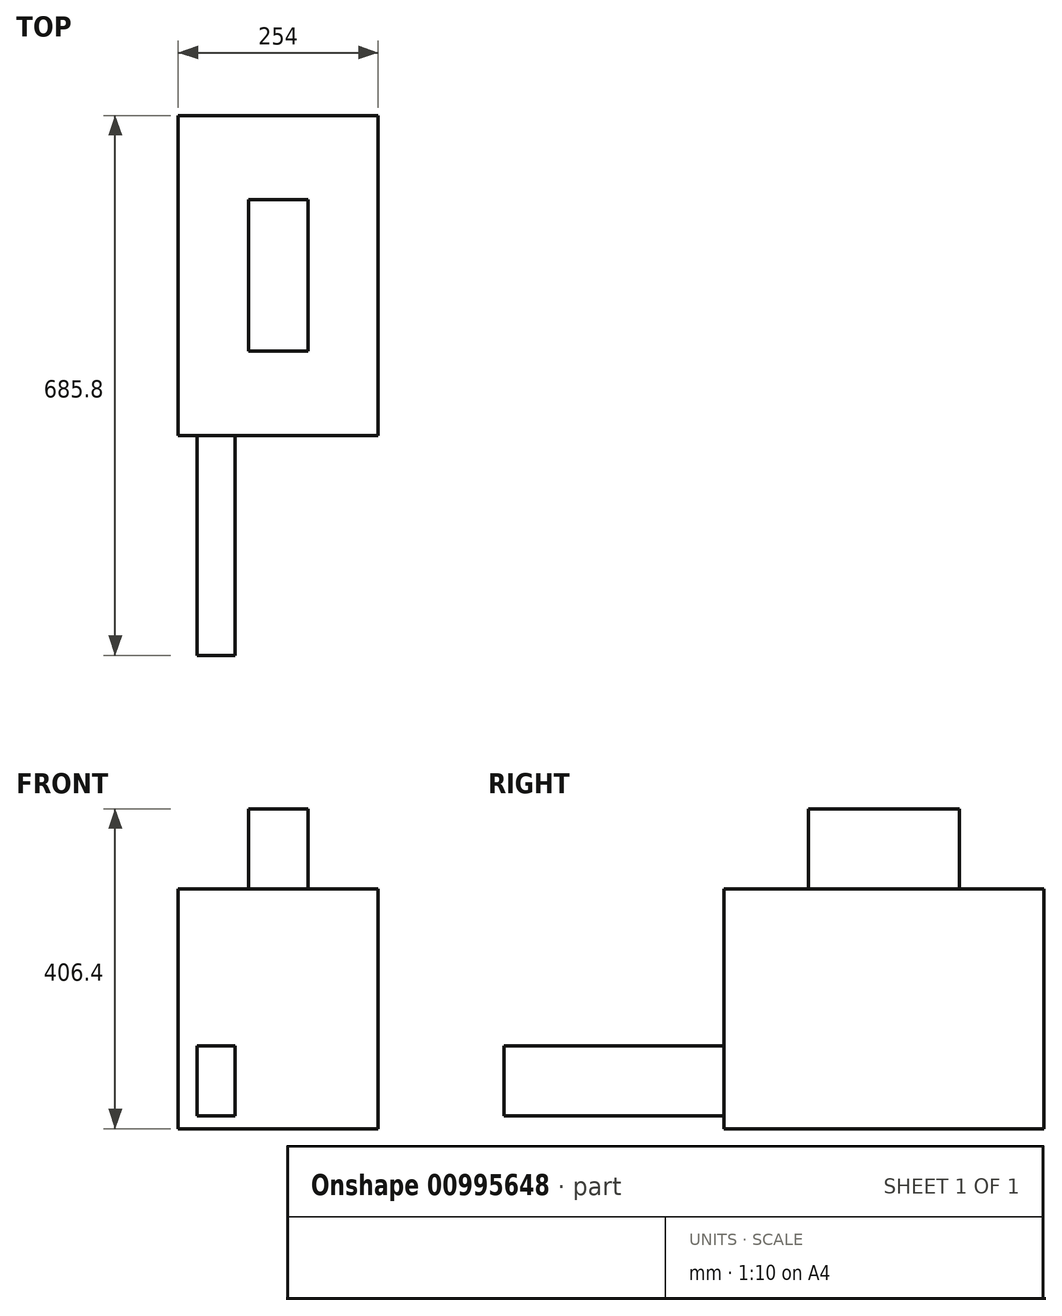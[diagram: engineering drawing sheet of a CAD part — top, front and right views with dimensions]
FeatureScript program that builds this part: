
annotation { "Feature Type Name" : "Feature", "Feature Type Description" : "" }
export const myFeature = defineFeature(function(context is Context, id is Id, definition is map)
    precondition{}
    {
        {
            var Q0;
            Q0=qCreatedBy(makeId("Top.planeOp"),FACE);
            var sketch = newSketch(context, id + "F0", { "sketchPlane" : qUnion([Q0])});
            skLineSegment(sketch, "E0.bottom", {"start": v(127, -203.2) * mm, "end": v(-127, -203.2) * mm});
            skLineSegment(sketch, "E0.top", {"start": v(127, 203.2) * mm, "end": v(-127, 203.2) * mm});
            skLineSegment(sketch, "E0.left", {"start": v(127, -203.2) * mm, "end": v(127, 203.2) * mm});
            skLineSegment(sketch, "E0.right", {"start": v(-127, -203.2) * mm, "end": v(-127, 203.2) * mm});
            skPoint(sketch, "E0.middle", {"position": v(0, 0) * mm});
            skSolve(sketch);
        }
        {
            var Q0;
            Q0 = qSketchRegion(id + "F0", true);
            extrude(context, id + "F1", {"entities" : qUnion([Q0]), "depth" : 304.8 * mm, "offsetDistance" : 25.4 * mm});
        }
        {
            var Q0;
            Q0=makeQuery(id+"F1.opExtrude","SWEPT_FACE",FACE,{"disambiguationData":[OSD([sQuery(id+"F0.wireOp",EDGE,"E0.bottom")])]});
            var sketch = newSketch(context, id + "F2", { "sketchPlane" : qUnion([Q0])});
            skLineSegment(sketch, "E1.bottom", {"start": v(-55, 16.19) * mm, "end": v(-103.23, 16.19) * mm});
            skLineSegment(sketch, "E1.top", {"start": v(-55, 105.28) * mm, "end": v(-103.23, 105.28) * mm});
            skLineSegment(sketch, "E1.left", {"start": v(-55, 16.19) * mm, "end": v(-55, 105.28) * mm});
            skLineSegment(sketch, "E1.right", {"start": v(-103.23, 16.19) * mm, "end": v(-103.23, 105.28) * mm});
            skPoint(sketch, "E1.middle", {"position": v(-79.12, 60.73) * mm});
            skSolve(sketch);
        }
        {
            var Q0;
            Q0=makeQuery(id+"F2.imprint","IMPRINT",FACE,{"disambiguationData":[TD([[makeQuery(id+"F2.imprint","IMPRINT",EDGE,{"derivedFrom":sQuery(id+"F2.wireOp",EDGE,"E1.bottom")}),-1.0]])]});
            extrude(context, id + "F3", {"entities" : qUnion([Q0]), "operationType" : NewBodyOperationType.ADD, "depth" : 279.4 * mm, "offsetDistance" : 25.4 * mm});
        }
        {
            var Q0;
            Q0=makeQuery(id+"F1.opExtrude","CAP_FACE",FACE,{"disambiguationData":[OSD([sQuery(id+"F0.wireOp",EDGE,"E0.bottom"),sQuery(id+"F0.wireOp",EDGE,"E0.top"),sQuery(id+"F0.wireOp",EDGE,"E0.left"),sQuery(id+"F0.wireOp",EDGE,"E0.right")])],"isStart":false});
            var sketch = newSketch(context, id + "F4", { "sketchPlane" : qUnion([Q0])});
            skLineSegment(sketch, "E2.bottom", {"start": v(37.7, -96.02) * mm, "end": v(-37.7, -96.02) * mm});
            skLineSegment(sketch, "E2.top", {"start": v(37.7, 96.02) * mm, "end": v(-37.7, 96.02) * mm});
            skLineSegment(sketch, "E2.left", {"start": v(37.7, -96.02) * mm, "end": v(37.7, 96.02) * mm});
            skLineSegment(sketch, "E2.right", {"start": v(-37.7, -96.02) * mm, "end": v(-37.7, 96.02) * mm});
            skPoint(sketch, "E2.middle", {"position": v(0, 0) * mm});
            skSolve(sketch);
        }
        {
            var Q0;
            Q0=makeQuery(id+"F4.imprint","IMPRINT",FACE,{"disambiguationData":[TD([[makeQuery(id+"F4.imprint","IMPRINT",EDGE,{"derivedFrom":sQuery(id+"F4.wireOp",EDGE,"E2.bottom")}),-1.0]])]});
            extrude(context, id + "F5", {"entities" : qUnion([Q0]), "operationType" : NewBodyOperationType.ADD, "depth" : 101.6 * mm, "offsetDistance" : 25.4 * mm});
        }
    });
